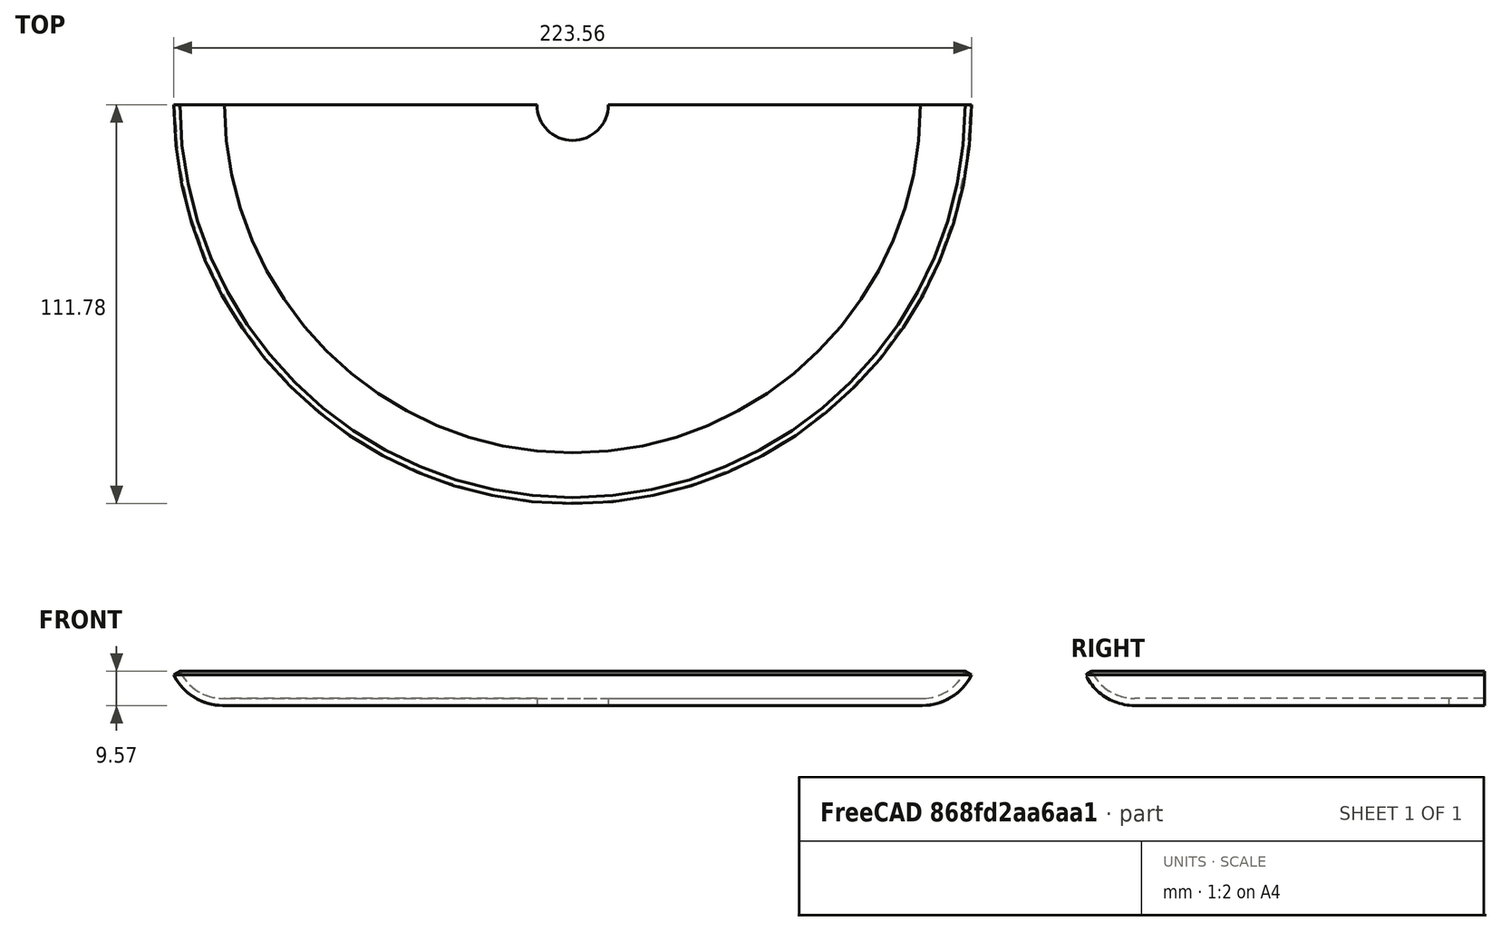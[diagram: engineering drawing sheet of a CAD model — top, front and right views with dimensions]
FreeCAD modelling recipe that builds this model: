
FCSTD DOCUMENT  (FreeCAD 0.18R16110 (Git))
Label: savoniousextend
License: All rights reserved
LicenseURL: http://en.wikipedia.org/wiki/All_rights_reserved
objects: Sketcher::SketchObject×1, PartDesign::Revolution×1, PartDesign::Body×1, Part::Fillet×1
note: 5 computed .brp shape members not serialized (recipe doc carries the construction recipe); baked Part::Feature solids carry a one-line shape summary decoded from their .brp

FEATURE [Sketcher::SketchObject] Sketch
  MapMode = 5
  Placement = pos=(0,0,0) rot=(1,0,0;1.5708rad)
  Support = -> [XZ_Plane]
  sketch-geometry (6):
    g0: LineSegment StartX=-10 StartY=0 StartZ=0 EndX=-97.8936 EndY=0 EndZ=0
    g1: ArcOfCircle CenterX=-98.0398 CenterY=15.2888 CenterZ=0 NormalX=0 NormalY=0 NormalZ=1 AngleXU=0 Radius=15.2895 StartAngle=3.5955 EndAngle=4.72195
    g2: LineSegment StartX=-111.781 StartY=8.58472 StartZ=0 EndX=-110.041 EndY=9.56979 EndZ=0
    g3: LineSegment StartX=-10 StartY=2.00432 StartZ=0 EndX=-97.5423 EndY=2.00432 EndZ=0
    g4: ArcOfCircle CenterX=-98.0398 CenterY=15.2888 CenterZ=0 NormalX=0 NormalY=0 NormalZ=1 AngleXU=0 Radius=13.2938 StartAngle=3.58631 EndAngle=4.74982
    g5: LineSegment StartX=-10 StartY=2.00432 StartZ=0 EndX=-10 EndY=0 EndZ=0
  constraints (13):
    c: PointOnObject(g0,g-1)
    c: Coincident(g1,g0)
    c: Coincident(g2,g1)
    c: Horizontal(g3)
    c: Distance(g2) = 2
    c: Coincident(g4,g1)
    c: Coincident(g4,g3)
    c: Coincident(g4,g2)
    c: DistanceX(g0) = -10
    c: DistanceX(g3) = -10
    c: Horizontal(g0)
    c: Coincident(g5,g3)
    c: Coincident(g5,g0)
FEATURE [PartDesign::Revolution] Revolution
  Angle = 180
  Axis = (0,2e-16,1)
  Base = (0,0,0)
  Placement = pos=(0,0,0) rot=(1,0,0;1.5708rad)
  Profile = -> Sketch
  ReferenceAxis = -> Sketch [V_Axis]
FEATURE [PartDesign::Body] Body
  Group = -> [Sketch,Revolution]
  Origin = -> Origin
  Tip = -> Revolution
FEATURE [Part::Fillet] Fillet
  Base = -> Revolution
  Edges = 4 edges r=0.5: [Edge8,Edge11,Edge12,Edge13]
